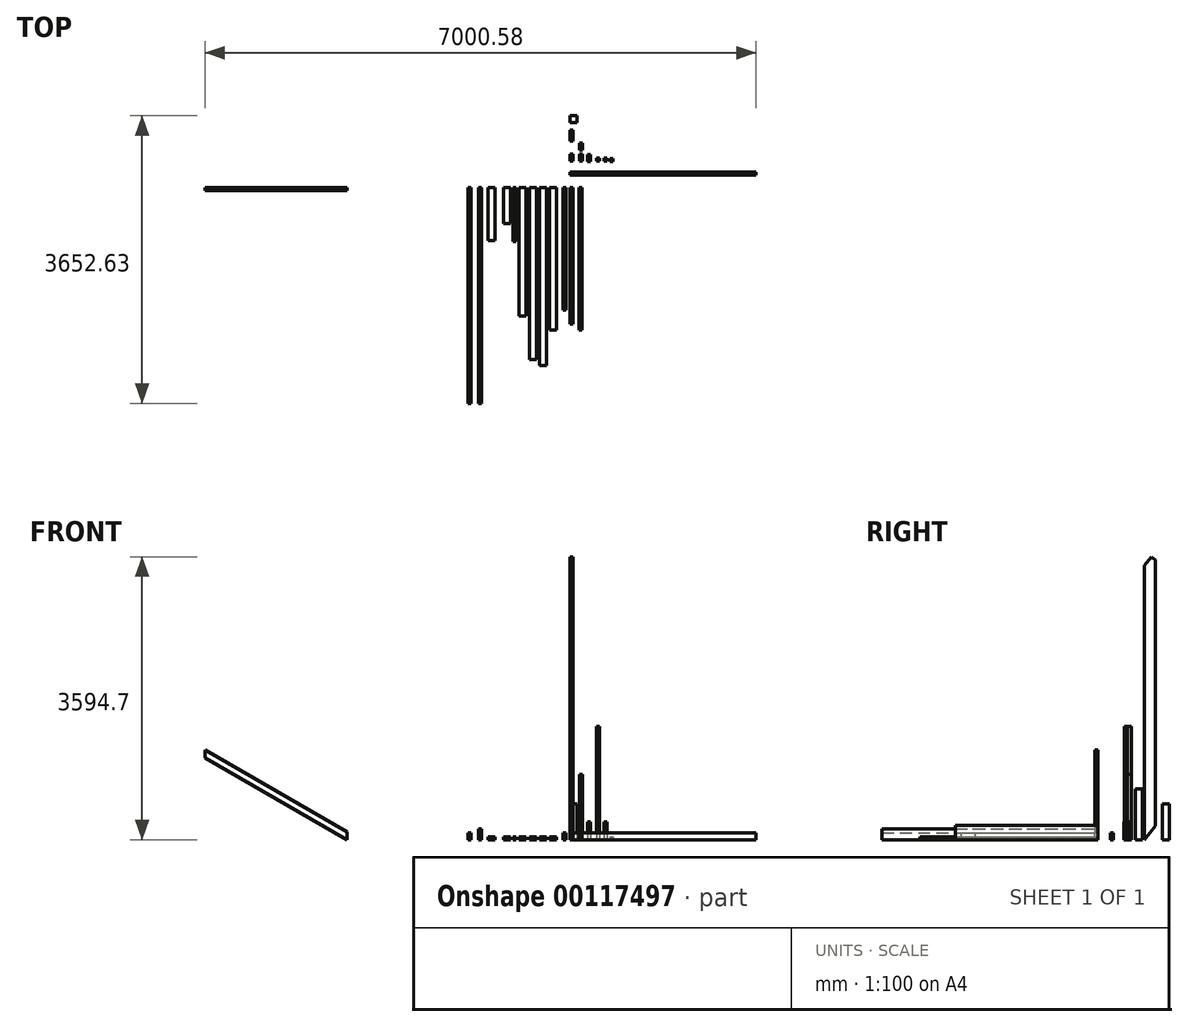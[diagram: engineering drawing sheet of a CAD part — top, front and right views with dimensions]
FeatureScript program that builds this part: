
annotation { "Feature Type Name" : "Feature", "Feature Type Description" : "" }
export const myFeature = defineFeature(function(context is Context, id is Id, definition is map)
    precondition{}
    {
        {
            var Q0;
            Q0=qCreatedBy(makeId("Front.planeOp"),FACE);
            var sketch = newSketch(context, id + "F0", { "sketchPlane" : qUnion([Q0])});
            skLineSegment(sketch, "E0.bottom", {"start": v(0, 0) * mm, "end": v(38.1, 0) * mm});
            skLineSegment(sketch, "E0.top", {"start": v(0, 88.9) * mm, "end": v(38.1, 88.9) * mm});
            skLineSegment(sketch, "E0.left", {"start": v(0, 0) * mm, "end": v(0, 88.9) * mm});
            skLineSegment(sketch, "E0.right", {"start": v(38.1, 0) * mm, "end": v(38.1, 88.9) * mm});
            skSolve(sketch);
        }
        {
            var Q0;
            Q0=makeQuery(id+"F0.imprint","IMPRINT",FACE,{"disambiguationData":[TD([[makeQuery(id+"F0.imprint","IMPRINT",EDGE,{"derivedFrom":sQuery(id+"F0.wireOp",EDGE,"E0.bottom")}),1.0]])]});
            extrude(context, id + "F1", {"entities" : qUnion([Q0]), "depth" : 1733.55 * mm});
        }
        {
            var Q0;
            Q0=qCreatedBy(makeId("Front.planeOp"),FACE);
            var sketch = newSketch(context, id + "F2", { "sketchPlane" : qUnion([Q0])});
            skLineSegment(sketch, "E1.bottom", {"start": v(113.1, 0) * mm, "end": v(151.2, 0) * mm});
            skLineSegment(sketch, "E1.top", {"start": v(113.1, 184.15) * mm, "end": v(151.2, 184.15) * mm});
            skLineSegment(sketch, "E1.left", {"start": v(113.1, 0) * mm, "end": v(113.1, 184.15) * mm});
            skLineSegment(sketch, "E1.right", {"start": v(151.2, 0) * mm, "end": v(151.2, 184.15) * mm});
            skSolve(sketch);
        }
        {
            var Q0;
            Q0=makeQuery(id+"F2.imprint","IMPRINT",FACE,{"disambiguationData":[TD([[makeQuery(id+"F2.imprint","IMPRINT",EDGE,{"derivedFrom":sQuery(id+"F2.wireOp",EDGE,"E1.bottom")}),1.0]])]});
            extrude(context, id + "F3", {"entities" : qUnion([Q0]), "depth" : 1809.75 * mm});
        }
        {
            var Q0;
            Q0=qCreatedBy(makeId("Front.planeOp"),FACE);
            var sketch = newSketch(context, id + "F4", { "sketchPlane" : qUnion([Q0])});
            skLineSegment(sketch, "E2.bottom", {"start": v(-51.28, 0) * mm, "end": v(-89.38, 0) * mm});
            skLineSegment(sketch, "E2.top", {"start": v(-51.28, 88.9) * mm, "end": v(-89.38, 88.9) * mm});
            skLineSegment(sketch, "E2.left", {"start": v(-51.28, 0) * mm, "end": v(-51.28, 88.9) * mm});
            skLineSegment(sketch, "E2.right", {"start": v(-89.38, 0) * mm, "end": v(-89.38, 88.9) * mm});
            skSolve(sketch);
        }
        {
            var Q0;
            Q0=makeQuery(id+"F4.imprint","IMPRINT",FACE,{"disambiguationData":[TD([[makeQuery(id+"F4.imprint","IMPRINT",EDGE,{"derivedFrom":sQuery(id+"F4.wireOp",EDGE,"E2.bottom")}),-1.0]])]});
            extrude(context, id + "F5", {"entities" : qUnion([Q0]), "depth" : 1555.75 * mm});
        }
        {
            var Q0;
            Q0=qCreatedBy(makeId("Right.planeOp"),FACE);
            var sketch = newSketch(context, id + "F6", { "sketchPlane" : qUnion([Q0])});
            skLineSegment(sketch, "E3.bottom", {"start": v(154.38, 0) * mm, "end": v(192.48, 0) * mm});
            skLineSegment(sketch, "E3.top", {"start": v(154.38, 88.9) * mm, "end": v(192.48, 88.9) * mm});
            skLineSegment(sketch, "E3.left", {"start": v(154.38, 0) * mm, "end": v(154.38, 88.9) * mm});
            skLineSegment(sketch, "E3.right", {"start": v(192.48, 0) * mm, "end": v(192.48, 88.9) * mm});
            skSolve(sketch);
        }
        {
            var Q0;
            Q0=makeQuery(id+"F6.imprint","IMPRINT",FACE,{"disambiguationData":[TD([[makeQuery(id+"F6.imprint","IMPRINT",EDGE,{"derivedFrom":sQuery(id+"F6.wireOp",EDGE,"E3.bottom")}),1.0]])]});
            extrude(context, id + "F7", {"entities" : qUnion([Q0]), "depth" : 2362.2 * mm});
        }
        {
            var Q0;
            Q0=qCreatedBy(makeId("Front.planeOp"),FACE);
            var sketch = newSketch(context, id + "F8", { "sketchPlane" : qUnion([Q0])});
            skLineSegment(sketch, "E4.bottom", {"start": v(-172.83, 0) * mm, "end": v(-261.73, 0) * mm});
            skLineSegment(sketch, "E4.top", {"start": v(-172.83, 38.1) * mm, "end": v(-261.73, 38.1) * mm});
            skLineSegment(sketch, "E4.left", {"start": v(-172.83, 0) * mm, "end": v(-172.83, 38.1) * mm});
            skLineSegment(sketch, "E4.right", {"start": v(-261.73, 0) * mm, "end": v(-261.73, 38.1) * mm});
            skSolve(sketch);
        }
        {
            var Q0;
            Q0=makeQuery(id+"F8.imprint","IMPRINT",FACE,{"disambiguationData":[TD([[makeQuery(id+"F8.imprint","IMPRINT",EDGE,{"derivedFrom":sQuery(id+"F8.wireOp",EDGE,"E4.bottom")}),-1.0]])]});
            extrude(context, id + "F9", {"entities" : qUnion([Q0]), "depth" : 1809.75 * mm});
        }
        {
            var Q0;
            Q0=qCreatedBy(makeId("Front.planeOp"),FACE);
            var sketch = newSketch(context, id + "F10", { "sketchPlane" : qUnion([Q0])});
            skLineSegment(sketch, "E5.bottom", {"start": v(-302.3, 0) * mm, "end": v(-391.2, 0) * mm});
            skLineSegment(sketch, "E5.top", {"start": v(-302.3, 38.1) * mm, "end": v(-391.2, 38.1) * mm});
            skLineSegment(sketch, "E5.left", {"start": v(-302.3, 0) * mm, "end": v(-302.3, 38.1) * mm});
            skLineSegment(sketch, "E5.right", {"start": v(-391.2, 0) * mm, "end": v(-391.2, 38.1) * mm});
            skSolve(sketch);
        }
        {
            var Q0;
            Q0=makeQuery(id+"F10.imprint","IMPRINT",FACE,{"disambiguationData":[TD([[makeQuery(id+"F10.imprint","IMPRINT",EDGE,{"derivedFrom":sQuery(id+"F10.wireOp",EDGE,"E5.bottom")}),-1.0]])]});
            extrude(context, id + "F11", {"entities" : qUnion([Q0]), "depth" : 2260.6 * mm});
        }
        {
            var Q0;
            Q0=qCreatedBy(makeId("Top.planeOp"),FACE);
            var sketch = newSketch(context, id + "F12", { "sketchPlane" : qUnion([Q0])});
            skLineSegment(sketch, "E6.bottom", {"start": v(0, 331.77) * mm, "end": v(38.1, 331.77) * mm});
            skLineSegment(sketch, "E6.top", {"start": v(0, 420.67) * mm, "end": v(38.1, 420.67) * mm});
            skLineSegment(sketch, "E6.left", {"start": v(0, 331.77) * mm, "end": v(0, 420.67) * mm});
            skLineSegment(sketch, "E6.right", {"start": v(38.1, 331.77) * mm, "end": v(38.1, 420.67) * mm});
            skSolve(sketch);
        }
        {
            var Q0;
            Q0=makeQuery(id+"F12.imprint","IMPRINT",FACE,{"disambiguationData":[TD([[makeQuery(id+"F12.imprint","IMPRINT",EDGE,{"derivedFrom":sQuery(id+"F12.wireOp",EDGE,"E6.bottom")}),1.0]])]});
            extrude(context, id + "F13", {"entities" : qUnion([Q0]), "depth" : 1441.45 * mm});
        }
        {
            var Q0;
            Q0=qCreatedBy(makeId("Top.planeOp"),FACE);
            var sketch = newSketch(context, id + "F14", { "sketchPlane" : qUnion([Q0])});
            skLineSegment(sketch, "E7.bottom", {"start": v(0, 590.01) * mm, "end": v(38.1, 590.01) * mm});
            skLineSegment(sketch, "E7.top", {"start": v(0, 729.71) * mm, "end": v(38.1, 729.71) * mm});
            skLineSegment(sketch, "E7.left", {"start": v(0, 590.01) * mm, "end": v(0, 729.71) * mm});
            skLineSegment(sketch, "E7.right", {"start": v(38.1, 590.01) * mm, "end": v(38.1, 729.71) * mm});
            skSolve(sketch);
        }
        {
            var Q0;
            Q0=makeQuery(id+"F14.imprint","IMPRINT",FACE,{"disambiguationData":[TD([[makeQuery(id+"F14.imprint","IMPRINT",EDGE,{"derivedFrom":sQuery(id+"F14.wireOp",EDGE,"E7.bottom")}),1.0]])]});
            extrude(context, id + "F15", {"entities" : qUnion([Q0]), "depth" : 3657.6 * mm});
        }
        {
            var Q0;
            Q0=makeQuery(id+"F15.opExtrude","SWEPT_FACE",FACE,{"disambiguationData":[OSD([sQuery(id+"F14.wireOp",EDGE,"E7.left")])]});
            var sketch = newSketch(context, id + "F16", { "sketchPlane" : qUnion([Q0])});
            skLineSegment(sketch, "E8", {"start": v(-590.01, 0) * mm, "end": v(-729.71, 172.52) * mm});
            skLineSegment(sketch, "E9", {"start": v(-729.71, 172.52) * mm, "end": v(-729.71, 0) * mm});
            skLineSegment(sketch, "E10", {"start": v(-729.71, 0) * mm, "end": v(-590.01, 0) * mm});
            skLineSegment(sketch, "E11", {"start": v(-729.71, 3657.6) * mm, "end": v(-590.01, 3657.6) * mm});
            skLineSegment(sketch, "E12", {"start": v(-590.01, 3657.6) * mm, "end": v(-590.01, 3485.08) * mm});
            skLineSegment(sketch, "E13", {"start": v(-590.01, 3485.08) * mm, "end": v(-729.71, 3657.6) * mm});
            skSolve(sketch);
        }
        {
            var Q0;
            Q0=makeQuery(id+"F16.imprint","IMPRINT",FACE,{"disambiguationData":[TD([[makeQuery(id+"F16.imprint","IMPRINT",EDGE,{"derivedFrom":sQuery(id+"F16.wireOp",EDGE,"E11")}),1.0]])]});
            var Q1;
            Q1=makeQuery(id+"F16.imprint","IMPRINT",FACE,{"disambiguationData":[TD([[makeQuery(id+"F16.imprint","IMPRINT",EDGE,{"derivedFrom":sQuery(id+"F16.wireOp",EDGE,"E8")}),1.0]])]});
            extrude(context, id + "F17", {"entities" : qUnion([Q0, Q1]), "operationType" : NewBodyOperationType.REMOVE, "oppositeDirection" : true, "depth" : 38.1 * mm});
        }
        {
            var Q0;
            Q0=makeQuery(id+"F15.opExtrude","SWEPT_FACE",FACE,{"disambiguationData":[OSD([sQuery(id+"F14.wireOp",EDGE,"E7.left")])]});
            var sketch = newSketch(context, id + "F18", { "sketchPlane" : qUnion([Q0])});
            skLineSegment(sketch, "E14", {"start": v(-729.71, 3657.6) * mm, "end": v(-677.93, 3593.65) * mm});
            skLineSegment(sketch, "E15", {"start": v(-677.93, 3593.65) * mm, "end": v(-729.71, 3551.72) * mm});
            skLineSegment(sketch, "E16", {"start": v(-729.71, 3551.72) * mm, "end": v(-729.71, 3657.6) * mm});
            skSolve(sketch);
        }
        {
            var Q0;
            Q0=makeQuery(id+"F18.imprint","IMPRINT",FACE,{"disambiguationData":[TD([[makeQuery(id+"F18.imprint","IMPRINT",EDGE,{"derivedFrom":sQuery(id+"F18.wireOp",EDGE,"E14")}),1.0]])]});
            extrude(context, id + "F19", {"entities" : qUnion([Q0]), "operationType" : NewBodyOperationType.REMOVE, "oppositeDirection" : true, "depth" : 38.1 * mm});
        }
        {
            var Q0;
            Q0=qCreatedBy(makeId("Front.planeOp"),FACE);
            var sketch = newSketch(context, id + "F20", { "sketchPlane" : qUnion([Q0])});
            skLineSegment(sketch, "E17.bottom", {"start": v(-428.23, 0) * mm, "end": v(-517.13, 0) * mm});
            skLineSegment(sketch, "E17.top", {"start": v(-428.23, 38.1) * mm, "end": v(-517.13, 38.1) * mm});
            skLineSegment(sketch, "E17.left", {"start": v(-428.23, 0) * mm, "end": v(-428.23, 38.1) * mm});
            skLineSegment(sketch, "E17.right", {"start": v(-517.13, 0) * mm, "end": v(-517.13, 38.1) * mm});
            skSolve(sketch);
        }
        {
            var Q0;
            Q0=makeQuery(id+"F20.imprint","IMPRINT",FACE,{"disambiguationData":[TD([[makeQuery(id+"F20.imprint","IMPRINT",EDGE,{"derivedFrom":sQuery(id+"F20.wireOp",EDGE,"E17.bottom")}),-1.0]])]});
            extrude(context, id + "F21", {"entities" : qUnion([Q0]), "depth" : 2184.4 * mm});
        }
        {
            var Q0;
            Q0=qCreatedBy(makeId("Front.planeOp"),FACE);
            var sketch = newSketch(context, id + "F22", { "sketchPlane" : qUnion([Q0])});
            skLineSegment(sketch, "E18.bottom", {"start": v(-564, 0) * mm, "end": v(-652.9, 0) * mm});
            skLineSegment(sketch, "E18.top", {"start": v(-564, 38.1) * mm, "end": v(-652.9, 38.1) * mm});
            skLineSegment(sketch, "E18.left", {"start": v(-564, 0) * mm, "end": v(-564, 38.1) * mm});
            skLineSegment(sketch, "E18.right", {"start": v(-652.9, 0) * mm, "end": v(-652.9, 38.1) * mm});
            skSolve(sketch);
        }
        {
            var Q0;
            Q0=makeQuery(id+"F22.imprint","IMPRINT",FACE,{"disambiguationData":[TD([[makeQuery(id+"F22.imprint","IMPRINT",EDGE,{"derivedFrom":sQuery(id+"F22.wireOp",EDGE,"E18.bottom")}),-1.0]])]});
            extrude(context, id + "F23", {"entities" : qUnion([Q0]), "depth" : 1631.95 * mm});
        }
        {
            var Q0;
            Q0=qCreatedBy(makeId("Top.planeOp"),FACE);
            var sketch = newSketch(context, id + "F24", { "sketchPlane" : qUnion([Q0])});
            skLineSegment(sketch, "E19.bottom", {"start": v(117.14, 331.81) * mm, "end": v(155.24, 331.81) * mm});
            skLineSegment(sketch, "E19.top", {"start": v(117.14, 420.71) * mm, "end": v(155.24, 420.71) * mm});
            skLineSegment(sketch, "E19.left", {"start": v(117.14, 331.81) * mm, "end": v(117.14, 420.71) * mm});
            skLineSegment(sketch, "E19.right", {"start": v(155.24, 331.81) * mm, "end": v(155.24, 420.71) * mm});
            skSolve(sketch);
        }
        {
            var Q0;
            Q0=makeQuery(id+"F24.imprint","IMPRINT",FACE,{"disambiguationData":[TD([[makeQuery(id+"F24.imprint","IMPRINT",EDGE,{"derivedFrom":sQuery(id+"F24.wireOp",EDGE,"E19.bottom")}),1.0]])]});
            extrude(context, id + "F25", {"entities" : qUnion([Q0]), "depth" : 831.85 * mm});
        }
        {
            var Q0;
            Q0=qCreatedBy(makeId("Top.planeOp"),FACE);
            var sketch = newSketch(context, id + "F26", { "sketchPlane" : qUnion([Q0])});
            skLineSegment(sketch, "E20.bottom", {"start": v(221.61, 329.21) * mm, "end": v(259.71, 329.21) * mm});
            skLineSegment(sketch, "E20.top", {"start": v(221.61, 418.11) * mm, "end": v(259.71, 418.11) * mm});
            skLineSegment(sketch, "E20.left", {"start": v(221.61, 329.21) * mm, "end": v(221.61, 418.11) * mm});
            skLineSegment(sketch, "E20.right", {"start": v(259.71, 329.21) * mm, "end": v(259.71, 418.11) * mm});
            skSolve(sketch);
        }
        {
            var Q0;
            Q0=makeQuery(id+"F26.imprint","IMPRINT",FACE,{"disambiguationData":[TD([[makeQuery(id+"F26.imprint","IMPRINT",EDGE,{"derivedFrom":sQuery(id+"F26.wireOp",EDGE,"E20.bottom")}),1.0]])]});
            extrude(context, id + "F27", {"entities" : qUnion([Q0]), "depth" : 228.6 * mm});
        }
        {
            var Q0;
            Q0=qCreatedBy(makeId("Top.planeOp"),FACE);
            var sketch = newSketch(context, id + "F28", { "sketchPlane" : qUnion([Q0])});
            skLineSegment(sketch, "E21.bottom", {"start": v(333.45, 332.24) * mm, "end": v(371.55, 332.24) * mm});
            skLineSegment(sketch, "E21.top", {"start": v(333.45, 370.34) * mm, "end": v(371.55, 370.34) * mm});
            skLineSegment(sketch, "E21.left", {"start": v(333.45, 332.24) * mm, "end": v(333.45, 370.34) * mm});
            skLineSegment(sketch, "E21.right", {"start": v(371.55, 332.24) * mm, "end": v(371.55, 370.34) * mm});
            skSolve(sketch);
        }
        {
            var Q0;
            Q0=makeQuery(id+"F28.imprint","IMPRINT",FACE,{"disambiguationData":[TD([[makeQuery(id+"F28.imprint","IMPRINT",EDGE,{"derivedFrom":sQuery(id+"F28.wireOp",EDGE,"E21.bottom")}),1.0]])]});
            extrude(context, id + "F29", {"entities" : qUnion([Q0]), "depth" : 1441.45 * mm});
        }
        {
            var Q0;
            Q0=qCreatedBy(makeId("Front.planeOp"),FACE);
            var sketch = newSketch(context, id + "F30", { "sketchPlane" : qUnion([Q0])});
            skLineSegment(sketch, "E22.bottom", {"start": v(-688.41, 0) * mm, "end": v(-726.51, 0) * mm});
            skLineSegment(sketch, "E22.top", {"start": v(-688.41, 38.1) * mm, "end": v(-726.51, 38.1) * mm});
            skLineSegment(sketch, "E22.left", {"start": v(-688.41, 0) * mm, "end": v(-688.41, 38.1) * mm});
            skLineSegment(sketch, "E22.right", {"start": v(-726.51, 0) * mm, "end": v(-726.51, 38.1) * mm});
            skSolve(sketch);
        }
        {
            var Q0;
            Q0=makeQuery(id+"F30.imprint","IMPRINT",FACE,{"disambiguationData":[TD([[makeQuery(id+"F30.imprint","IMPRINT",EDGE,{"derivedFrom":sQuery(id+"F30.wireOp",EDGE,"E22.bottom")}),-1.0]])]});
            extrude(context, id + "F31", {"entities" : qUnion([Q0]), "depth" : 685.8 * mm});
        }
        {
            var Q0;
            Q0=qCreatedBy(makeId("Front.planeOp"),FACE);
            var sketch = newSketch(context, id + "F32", { "sketchPlane" : qUnion([Q0])});
            skLineSegment(sketch, "E23.bottom", {"start": v(-760.55, 0) * mm, "end": v(-849.45, 0) * mm});
            skLineSegment(sketch, "E23.top", {"start": v(-760.55, 38.1) * mm, "end": v(-849.45, 38.1) * mm});
            skLineSegment(sketch, "E23.left", {"start": v(-760.55, 0) * mm, "end": v(-760.55, 38.1) * mm});
            skLineSegment(sketch, "E23.right", {"start": v(-849.45, 0) * mm, "end": v(-849.45, 38.1) * mm});
            skSolve(sketch);
        }
        {
            var Q0;
            Q0=makeQuery(id+"F32.imprint","IMPRINT",FACE,{"disambiguationData":[TD([[makeQuery(id+"F32.imprint","IMPRINT",EDGE,{"derivedFrom":sQuery(id+"F32.wireOp",EDGE,"E23.bottom")}),-1.0]])]});
            extrude(context, id + "F33", {"entities" : qUnion([Q0]), "depth" : 457.2 * mm});
        }
        {
            var Q0;
            Q0=qCreatedBy(makeId("Top.planeOp"),FACE);
            var sketch = newSketch(context, id + "F34", { "sketchPlane" : qUnion([Q0])});
            skLineSegment(sketch, "E24.bottom", {"start": v(0, 820.53) * mm, "end": v(88.9, 820.53) * mm});
            skLineSegment(sketch, "E24.top", {"start": v(0, 909.43) * mm, "end": v(88.9, 909.43) * mm});
            skLineSegment(sketch, "E24.left", {"start": v(0, 820.53) * mm, "end": v(0, 909.43) * mm});
            skLineSegment(sketch, "E24.right", {"start": v(88.9, 820.53) * mm, "end": v(88.9, 909.43) * mm});
            skSolve(sketch);
        }
        {
            var Q0;
            Q0=makeQuery(id+"F34.imprint","IMPRINT",FACE,{"disambiguationData":[TD([[makeQuery(id+"F34.imprint","IMPRINT",EDGE,{"derivedFrom":sQuery(id+"F34.wireOp",EDGE,"E24.bottom")}),1.0]])]});
            extrude(context, id + "F35", {"entities" : qUnion([Q0]), "depth" : 457.2 * mm});
        }
        {
            var Q0;
            Q0=qCreatedBy(makeId("Top.planeOp"),FACE);
            var sketch = newSketch(context, id + "F36", { "sketchPlane" : qUnion([Q0])});
            skLineSegment(sketch, "E25.bottom", {"start": v(432.23, 334.64) * mm, "end": v(470.33, 334.64) * mm});
            skLineSegment(sketch, "E25.top", {"start": v(432.23, 372.74) * mm, "end": v(470.33, 372.74) * mm});
            skLineSegment(sketch, "E25.left", {"start": v(432.23, 334.64) * mm, "end": v(432.23, 372.74) * mm});
            skLineSegment(sketch, "E25.right", {"start": v(470.33, 334.64) * mm, "end": v(470.33, 372.74) * mm});
            skSolve(sketch);
        }
        {
            var Q0;
            Q0=makeQuery(id+"F36.imprint","IMPRINT",FACE,{"disambiguationData":[TD([[makeQuery(id+"F36.imprint","IMPRINT",EDGE,{"derivedFrom":sQuery(id+"F36.wireOp",EDGE,"E25.bottom")}),1.0]])]});
            extrude(context, id + "F37", {"entities" : qUnion([Q0]), "depth" : 228.6 * mm});
        }
        {
            var Q0;
            Q0=qCreatedBy(makeId("Top.planeOp"),FACE);
            var sketch = newSketch(context, id + "F38", { "sketchPlane" : qUnion([Q0])});
            skLineSegment(sketch, "E26.bottom", {"start": v(506.3, 325.78) * mm, "end": v(544.4, 325.78) * mm});
            skLineSegment(sketch, "E26.top", {"start": v(506.3, 363.88) * mm, "end": v(544.4, 363.88) * mm});
            skLineSegment(sketch, "E26.left", {"start": v(506.3, 325.78) * mm, "end": v(506.3, 363.88) * mm});
            skLineSegment(sketch, "E26.right", {"start": v(544.4, 325.78) * mm, "end": v(544.4, 363.88) * mm});
            skSolve(sketch);
        }
        {
            var Q0;
            Q0 = qSketchRegion(id + "F38", true);
            extrude(context, id + "F39", {"entities" : qUnion([Q0]), "depth" : 38.1 * mm});
        }
        {
            var Q0;
            Q0=qCreatedBy(makeId("Front.planeOp"),FACE);
            var sketch = newSketch(context, id + "F40", { "sketchPlane" : qUnion([Q0])});
            skLineSegment(sketch, "E27", {"start": v(-2834.62, -1.05) * mm, "end": v(-4638.38, 1040.35) * mm});
            skLineSegment(sketch, "E28", {"start": v(-4638.38, 1040.35) * mm, "end": v(-4638.38, 1143) * mm});
            skLineSegment(sketch, "E29", {"start": v(-4638.38, 1143) * mm, "end": v(-2834.62, 101.6) * mm});
            skLineSegment(sketch, "E30", {"start": v(-2834.62, -1.05) * mm, "end": v(-2834.62, 101.6) * mm});
            skSolve(sketch);
        }
        {
            var Q0;
            Q0=qCreatedBy(makeId("Front.planeOp"),FACE);
            var sketch = newSketch(context, id + "F41", { "sketchPlane" : qUnion([Q0])});
            skLineSegment(sketch, "E31.bottom", {"start": v(-951.81, 0) * mm, "end": v(-1040.71, 0) * mm});
            skLineSegment(sketch, "E31.top", {"start": v(-951.81, 38.1) * mm, "end": v(-1040.71, 38.1) * mm});
            skLineSegment(sketch, "E31.left", {"start": v(-951.81, 0) * mm, "end": v(-951.81, 38.1) * mm});
            skLineSegment(sketch, "E31.right", {"start": v(-1040.71, 0) * mm, "end": v(-1040.71, 38.1) * mm});
            skSolve(sketch);
        }
        {
            var Q0;
            Q0=makeQuery(id+"F41.imprint","IMPRINT",FACE,{"disambiguationData":[TD([[makeQuery(id+"F41.imprint","IMPRINT",EDGE,{"derivedFrom":sQuery(id+"F41.wireOp",EDGE,"E31.bottom")}),-1.0]])]});
            extrude(context, id + "F42", {"entities" : qUnion([Q0]), "depth" : 673.1 * mm});
        }
        {
            var Q0;
            Q0=qCreatedBy(makeId("Front.planeOp"),FACE);
            var sketch = newSketch(context, id + "F43", { "sketchPlane" : qUnion([Q0])});
            skLineSegment(sketch, "E32", {"start": v(-1123.88, 0) * mm, "end": v(-1123.88, 139.7) * mm});
            skLineSegment(sketch, "E33", {"start": v(-1123.88, 139.7) * mm, "end": v(-1161.98, 139.7) * mm});
            skLineSegment(sketch, "E34", {"start": v(-1161.98, 139.7) * mm, "end": v(-1161.98, 0) * mm});
            skLineSegment(sketch, "E35", {"start": v(-1161.98, 0) * mm, "end": v(-1123.88, 0) * mm});
            skSolve(sketch);
        }
        {
            var Q0;
            Q0=makeQuery(id+"F43.imprint","IMPRINT",FACE,{"disambiguationData":[TD([[makeQuery(id+"F43.imprint","IMPRINT",EDGE,{"derivedFrom":sQuery(id+"F43.wireOp",EDGE,"E32")}),1.0]])]});
            extrude(context, id + "F44", {"entities" : qUnion([Q0]), "depth" : 2743.2 * mm});
        }
        {
            var Q0;
            Q0=makeQuery(id+"F40.imprint","IMPRINT",FACE,{"disambiguationData":[TD([[makeQuery(id+"F40.imprint","IMPRINT",EDGE,{"derivedFrom":sQuery(id+"F40.wireOp",EDGE,"E27")}),-1.0]])]});
            extrude(context, id + "F45", {"entities" : qUnion([Q0]), "depth" : 38.1 * mm});
        }
        {
            var Q0;
            Q0=qCreatedBy(makeId("Front.planeOp"),FACE);
            var sketch = newSketch(context, id + "F46", { "sketchPlane" : qUnion([Q0])});
            skLineSegment(sketch, "E36.bottom", {"start": v(-1256.46, 0) * mm, "end": v(-1294.56, 0) * mm});
            skLineSegment(sketch, "E36.top", {"start": v(-1256.46, 88.9) * mm, "end": v(-1294.56, 88.9) * mm});
            skLineSegment(sketch, "E36.left", {"start": v(-1256.46, 0) * mm, "end": v(-1256.46, 88.9) * mm});
            skLineSegment(sketch, "E36.right", {"start": v(-1294.56, 0) * mm, "end": v(-1294.56, 88.9) * mm});
            skSolve(sketch);
        }
        {
            var Q0;
            Q0=makeQuery(id+"F46.imprint","IMPRINT",FACE,{"disambiguationData":[TD([[makeQuery(id+"F46.imprint","IMPRINT",EDGE,{"derivedFrom":sQuery(id+"F46.wireOp",EDGE,"E36.bottom")}),-1.0]])]});
            extrude(context, id + "F47", {"entities" : qUnion([Q0]), "depth" : 2743.2 * mm});
        }
        {
            var Q0;
            Q0=qCreatedBy(makeId("Top.planeOp"),FACE);
            var sketch = newSketch(context, id + "F48", { "sketchPlane" : qUnion([Q0])});
            skLineSegment(sketch, "E37.bottom", {"start": v(118.34, 473.4) * mm, "end": v(156.44, 473.4) * mm});
            skLineSegment(sketch, "E37.top", {"start": v(118.34, 562.3) * mm, "end": v(156.44, 562.3) * mm});
            skLineSegment(sketch, "E37.left", {"start": v(118.34, 473.4) * mm, "end": v(118.34, 562.3) * mm});
            skLineSegment(sketch, "E37.right", {"start": v(156.44, 473.4) * mm, "end": v(156.44, 562.3) * mm});
            skSolve(sketch);
        }
        {
            var Q0;
            Q0=makeQuery(id+"F48.imprint","IMPRINT",FACE,{"disambiguationData":[TD([[makeQuery(id+"F48.imprint","IMPRINT",EDGE,{"derivedFrom":sQuery(id+"F48.wireOp",EDGE,"E37.bottom")}),1.0]])]});
            extrude(context, id + "F49", {"entities" : qUnion([Q0]), "depth" : 647.7 * mm});
        }
    });
